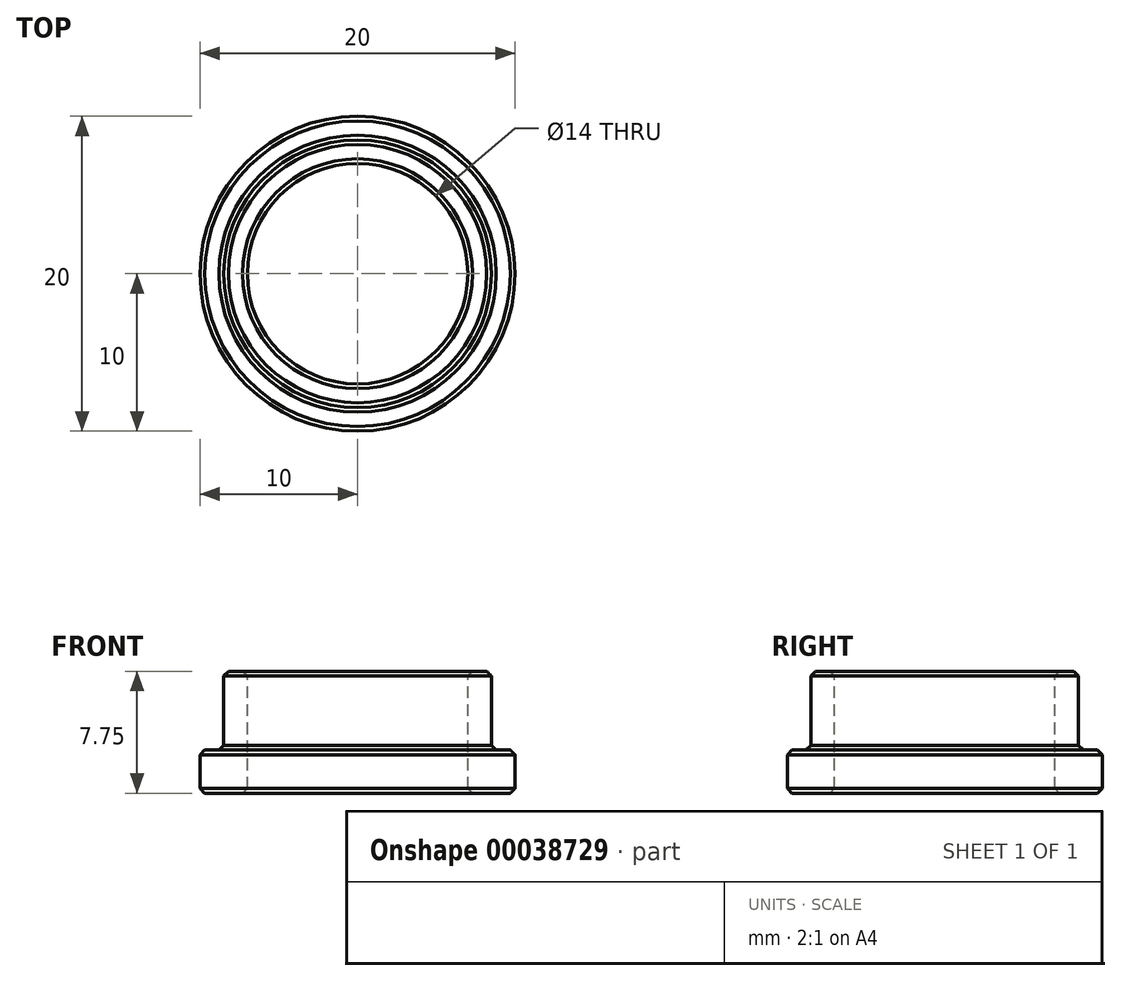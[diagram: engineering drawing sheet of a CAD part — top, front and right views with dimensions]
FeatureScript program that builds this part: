
annotation { "Feature Type Name" : "Feature", "Feature Type Description" : "" }
export const myFeature = defineFeature(function(context is Context, id is Id, definition is map)
    precondition{}
    {
        {
            var Q0;
            Q0=qCreatedBy(makeId("Top.planeOp"),FACE);
            var sketch = newSketch(context, id + "F0", { "sketchPlane" : qUnion([Q0])});
            skCircle(sketch, "E0", {"center": v(0, 0) * mm, "radius": 10 * mm});
            skSolve(sketch);
        }
        {
            var Q0;
            Q0 = qSketchRegion(id + "F0", true);
            extrude(context, id + "F1", {"entities" : qUnion([Q0]), "offsetDistance" : 25 * mm, "depth" : 2.75 * mm});
        }
        {
            var Q0;
            Q0=makeQuery(id+"F1.opExtrude","CAP_FACE",FACE,{"disambiguationData":[OSD([sQuery(id+"F0.wireOp",EDGE,"E0")])],"isStart":false});
            var sketch = newSketch(context, id + "F2", { "sketchPlane" : qUnion([Q0])});
            skCircle(sketch, "E1", {"center": v(0, 0) * mm, "radius": 8.5 * mm});
            skSolve(sketch);
        }
        {
            var Q0;
            Q0 = qSketchRegion(id + "F2", true);
            extrude(context, id + "F3", {"entities" : qUnion([Q0]), "operationType" : NewBodyOperationType.ADD, "depth" : 5 * mm});
        }
        {
            var Q0;
            Q0=makeQuery(id+"F3.opExtrude","CAP_FACE",FACE,{"disambiguationData":[OSD([sQuery(id+"F2.wireOp",EDGE,"E1")])],"isStart":false});
            var sketch = newSketch(context, id + "F4", { "sketchPlane" : qUnion([Q0])});
            skCircle(sketch, "E2", {"center": v(0, 0) * mm, "radius": 7 * mm});
            skSolve(sketch);
        }
        {
            var Q0;
            Q0 = qSketchRegion(id + "F4", true);
            extrude(context, id + "F5", {"entities" : qUnion([Q0]), "operationType" : NewBodyOperationType.REMOVE, "endBound" : BoundingType.THROUGH_ALL, "oppositeDirection" : true, "depth" : 25 * mm});
        }
        {
            var Q0;
            Q0=makeQuery(id+"F3.opExtrude","CAP_FACE",FACE,{"disambiguationData":[OSD([sQuery(id+"F2.wireOp",EDGE,"E1")])],"isStart":false});
            var Q1;
            Q1=makeQuery(id+"F1.opExtrude","CAP_FACE",FACE,{"disambiguationData":[OSD([sQuery(id+"F0.wireOp",EDGE,"E0")])],"isStart":false});
            var Q2;
            Q2=makeQuery(id+"F1.opExtrude","CAP_FACE",FACE,{"disambiguationData":[OSD([sQuery(id+"F0.wireOp",EDGE,"E0")])],"isStart":true});
            chamfer(context, id + "F6", {"entities" : qUnion([Q0, Q1, Q2]), "width" : 0.3 * mm, "tangentPropagation" : true});
        }
    });
